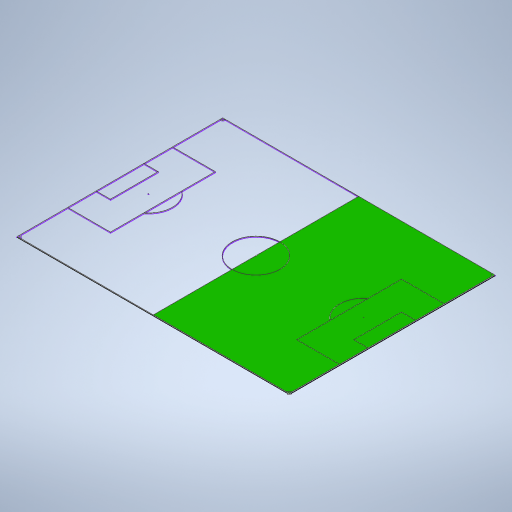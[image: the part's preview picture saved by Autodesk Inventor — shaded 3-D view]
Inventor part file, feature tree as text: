
AUTODESK INVENTOR PART (.ipt)
format: ipt  version: 2024.1 (Build 281209000, 209)  size: 523,776 bytes
history: native  units: in
note: dims shown in document units (in); Inventor stores cm internally (conversion verified against a paired STEP export)
features: extrude x42, sketch x1
ambient origin geometry x8: Origin, YZ Plane, XZ Plane, XY Plane, X Axis, Y Axis, Z Axis, Center Point
bodies: Solid3 (feature_tree), Solid4 (feature_tree), Solid5 (feature_tree), Solid6 (feature_tree), Solid7 (feature_tree), Solid8 (feature_tree), Solid9 (feature_tree), Solid10 (feature_tree), Solid11 (feature_tree)
feature tree (43):
  sketch  "Sketch2"  dims[d126=10.0in d127=0.0in d128=10.0in d129=0.0in d130=10.0in d131=0.0in d132=10.0in d133=0.0in d134=10.0in d135=0.0in d136=10.0in d137=0.0in d138=10.0in d139=0.0in d140=10.0in d141=0.0in d142=10.0in d143=0.0in d144=10.0in d145=0.0in d146=10.0in d147=0.0in d148=10.0in d149=0.0in d150=10.0in d151=0.0in d152=10.0in d153=0.0in d154=10.0in d155=0.0in d156=10.0in d157=0.0in d158=10.0in d159=0.0in d160=10.0in d161=0.0in d162=10.0in d163=0.0in d164=10.0in d165=0.0in d166=10.0in d167=0.0in d168=10.0in d169=0.0in d170=10.0in d171=0.0in d172=10.0in d173=0.0in d174=10.0in d175=0.0in d176=10.0in d177=0.0in d178=10.0in d179=0.0in d180=10.0in d181=0.0in d182=10.0in d183=0.0in d184=10.0in d185=0.0in d186=10.0in d187=0.0in d188=10.0in d189=0.0in d190=10.0in d191=0.0in d192=10.0in d193=0.0in d194=10.0in d195=0.0in d196=10.0in d197=0.0in d198=10.0in d199=0.0in d200=10.0in d201=0.0in d202=10.0in d203=0.0in d204=10.0in d205=0.0in d206=10.0in d207=0.0in d208=10.0in d209=0.0in]
  extrude  "Extrusion26"  Depth=10.0in TaperAngle=0.0deg
  extrude  "Extrusion27"  Depth=10.0in TaperAngle=0.0deg
  extrude  "Extrusion28"  Depth=10.0in TaperAngle=0.0deg
  extrude  "Extrusion29"  Depth=10.0in TaperAngle=0.0deg
  extrude  "Extrusion30"  Depth=10.0in TaperAngle=0.0deg
  extrude  "Extrusion31"  Depth=10.0in TaperAngle=0.0deg
  extrude  "Extrusion32"  Depth=10.0in TaperAngle=0.0deg
  extrude  "Extrusion33"  Depth=10.0in TaperAngle=0.0deg
  extrude  "Extrusion34"  Depth=10.0in TaperAngle=0.0deg
  extrude  "Extrusion35"  Depth=10.0in TaperAngle=0.0deg
  extrude  "Extrusion36"  Depth=10.0in TaperAngle=0.0deg
  extrude  "Extrusion37"  Depth=10.0in TaperAngle=0.0deg
  extrude  "Extrusion38"  Depth=10.0in TaperAngle=0.0deg
  extrude  "Extrusion39"  Depth=10.0in TaperAngle=0.0deg
  extrude  "Extrusion40"  Depth=10.0in TaperAngle=0.0deg
  extrude  "Extrusion41"  Depth=10.0in TaperAngle=0.0deg
  extrude  "Extrusion42"  Depth=10.0in TaperAngle=0.0deg
  extrude  "Extrusion43"  Depth=10.0in TaperAngle=0.0deg
  extrude  "Extrusion44"  Depth=10.0in TaperAngle=0.0deg
  extrude  "Extrusion45"  Depth=10.0in TaperAngle=0.0deg
  extrude  "Extrusion46"  Depth=10.0in TaperAngle=0.0deg
  extrude  "Extrusion47"  Depth=10.0in TaperAngle=0.0deg
  extrude  "Extrusion48"  Depth=10.0in TaperAngle=0.0deg
  extrude  "Extrusion49"  Depth=10.0in TaperAngle=0.0deg
  extrude  "Extrusion50"  Depth=10.0in TaperAngle=0.0deg
  extrude  "Extrusion51"  Depth=10.0in TaperAngle=0.0deg
  extrude  "Extrusion52"  Depth=10.0in TaperAngle=0.0deg
  extrude  "Extrusion53"  Depth=10.0in TaperAngle=0.0deg
  extrude  "Extrusion54"  Depth=10.0in TaperAngle=0.0deg
  extrude  "Extrusion55"  Depth=10.0in TaperAngle=0.0deg
  extrude  "Extrusion56"  Depth=10.0in TaperAngle=0.0deg
  extrude  "Extrusion57"  Depth=10.0in TaperAngle=0.0deg
  extrude  "Extrusion58"  Depth=10.0in TaperAngle=0.0deg
  extrude  "Extrusion59"  Depth=10.0in TaperAngle=0.0deg
  extrude  "Extrusion60"  Depth=10.0in TaperAngle=0.0deg
  extrude  "Extrusion61"  Depth=10.0in TaperAngle=0.0deg
  extrude  "Extrusion62"  Depth=10.0in TaperAngle=0.0deg
  extrude  "Extrusion63"  Depth=10.0in TaperAngle=0.0deg
  extrude  "Extrusion64"  Depth=10.0in TaperAngle=0.0deg
  extrude  "Extrusion65"  Depth=10.0in TaperAngle=0.0deg
  extrude  "Extrusion66"  Depth=10.0in TaperAngle=0.0deg
  extrude  "Extrusion67"  [1 undecoded]
note: 1 required parameter value undecoded (feature->parameter linkage not recoverable at this tier; creation-order binding heuristic only, values carry confidence <= 0.55)
